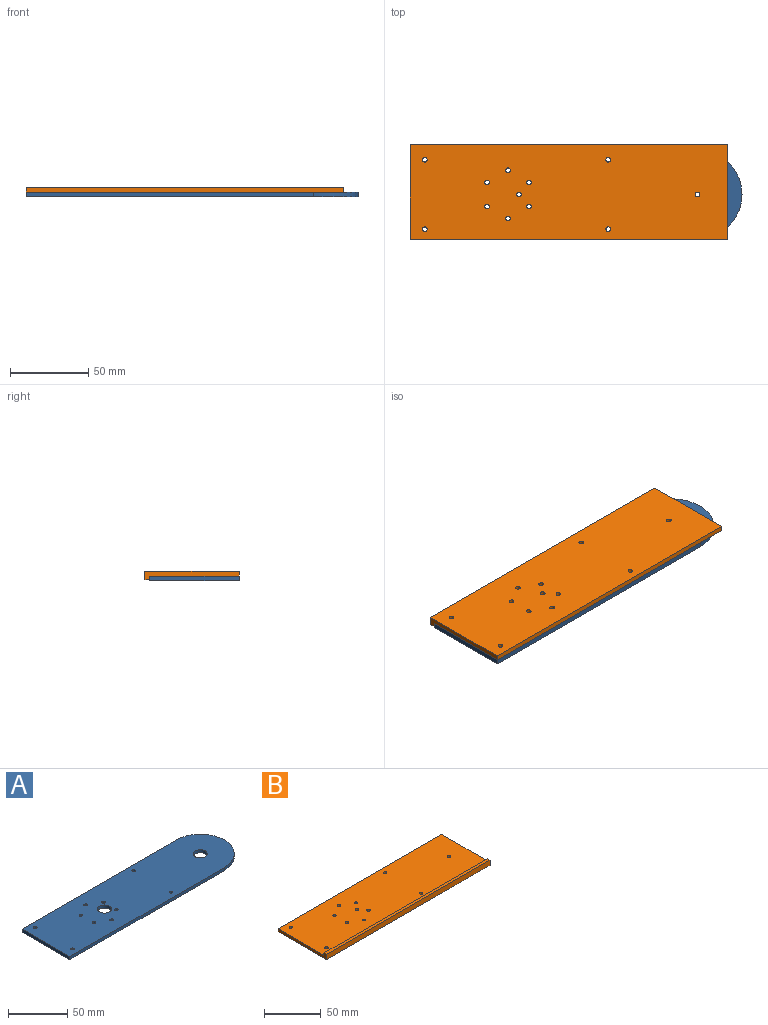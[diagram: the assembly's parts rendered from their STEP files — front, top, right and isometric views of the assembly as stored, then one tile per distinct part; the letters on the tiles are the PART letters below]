
ASSEMBLY  parts=2 mates=1
PART A: 18 faces, bbox 212.7x57.2x3.2 mm
  f0: plane 184.15x3.18mm, normal (0,-1,0), area 584.7mm2, adj f1,f3,f4,f5
  f1: cylinder r=28.57mm len=57.15mm, axis (0,0,-1), area 285mm2, adj f0,f2,f4,f5
  f2: plane 184.15x3.18mm, normal (0,1,0), area 584.7mm2, adj f1,f3,f4,f5
  f3: plane 57.15x3.18mm, normal (-1,0,0), area 181.5mm2, adj f0,f2,f4,f5
  f4: plane 212.73x57.15mm, normal (0,0,1), area 11512.4mm2, adj f0,f1,f2,f3,f6,f7,f8,f9
  f5: plane 212.73x57.15mm, normal (0,0,-1), area 11512.4mm2, adj f0,f1,f2,f3,f6,f7,f8,f9
  f6: cylinder r=1.47mm len=3.18mm, axis (0,0,-1), area 29.4mm2, adj f4,f5
  f7: cylinder r=1.47mm len=3.18mm, axis (0,0,-1), area 29.4mm2, adj f4,f5
  f8: cylinder r=1.47mm len=3.18mm, axis (0,0,-1), area 29.4mm2, adj f4,f5
  f9: cylinder r=1.47mm len=3.18mm, axis (0,0,-1), area 29.4mm2, adj f4,f5
  f10: cylinder r=1.47mm len=3.18mm, axis (0,0,-1), area 29.4mm2, adj f4,f5
  f11: cylinder r=1.47mm len=3.18mm, axis (0,0,-1), area 29.4mm2, adj f4,f5
  f12: cylinder r=1.47mm len=3.18mm, axis (0,0,-1), area 29.4mm2, adj f4,f5
  f13: cylinder r=1.47mm len=3.18mm, axis (0,0,-1), area 29.4mm2, adj f4,f5
  f14: cylinder r=1.47mm len=3.18mm, axis (0,0,-1), area 29.4mm2, adj f4,f5
  f15: cylinder r=1.47mm len=3.18mm, axis (0,0,-1), area 29.4mm2, adj f4,f5
  f16: cylinder r=6mm len=12mm, axis (0,0,-1), area 119.7mm2, adj f4,f5
  f17: cylinder r=6mm len=12mm, axis (0,0,-1), area 119.7mm2, adj f4,f5
PART B: 20 faces, bbox 203.2x60.3x5.6 mm
  f0: plane 203.2x3.18mm, normal (0,1,0), area 645.2mm2, adj f1,f2,f3,f4
  f1: plane 60.33x5.56mm, normal (-1,0,0), area 199.1mm2, adj f0,f3,f4,f17,f18,f19
  f2: plane 60.33x5.56mm, normal (1,0,0), area 199.1mm2, adj f0,f3,f4,f17,f18,f19
  f3: plane 203.2x57.15mm, normal (0,0,1), area 11531.1mm2, adj f0,f1,f2,f5,f6,f7,f8,f9
  f4: plane 203.2x60.33mm, normal (0,0,-1), area 12176.2mm2, adj f0,f1,f2,f5,f6,f7,f8,f9
  f5: cylinder r=1.47mm len=3.18mm, axis (0,0,-1), area 29.4mm2, adj f3,f4
  f6: cylinder r=1.47mm len=3.18mm, axis (0,0,-1), area 29.4mm2, adj f3,f4
  f7: cylinder r=1.47mm len=3.18mm, axis (0,0,-1), area 29.4mm2, adj f3,f4
  f8: cylinder r=1.47mm len=3.18mm, axis (0,0,-1), area 29.4mm2, adj f3,f4
  f9: cylinder r=1.47mm len=3.18mm, axis (0,0,-1), area 29.4mm2, adj f3,f4
  f10: cylinder r=1.47mm len=3.18mm, axis (0,0,-1), area 29.4mm2, adj f3,f4
  f11: cylinder r=1.47mm len=3.18mm, axis (0,0,-1), area 29.4mm2, adj f3,f4
  f12: cylinder r=1.47mm len=3.18mm, axis (0,0,-1), area 29.4mm2, adj f3,f4
  f13: cylinder r=1.47mm len=3.18mm, axis (0,0,-1), area 29.4mm2, adj f3,f4
  f14: cylinder r=1.47mm len=3.18mm, axis (0,0,-1), area 29.4mm2, adj f3,f4
  f15: cylinder r=1.47mm len=3.18mm, axis (0,0,-1), area 29.4mm2, adj f3,f4
  f16: cylinder r=1.47mm len=3.18mm, axis (0,0,-1), area 29.4mm2, adj f3,f4
  f17: plane 203.2x2.38mm, normal (0,1,0), area 483.9mm2, adj f1,f2,f3,f19
  f18: plane 203.2x5.56mm, normal (0,-1,0), area 1129mm2, adj f1,f2,f4,f19
  f19: plane 203.2x3.18mm, normal (0,0,1), area 645.2mm2, adj f1,f2,f17,f18
PLACE A at identity
PLACE B rot(axis=(1,0,0),180deg) t=(0,0,6.35)mm
MATE fastened B.f9 <-> A.f1  axis (0,0,-1) through (57.15,0,3.18)mm
